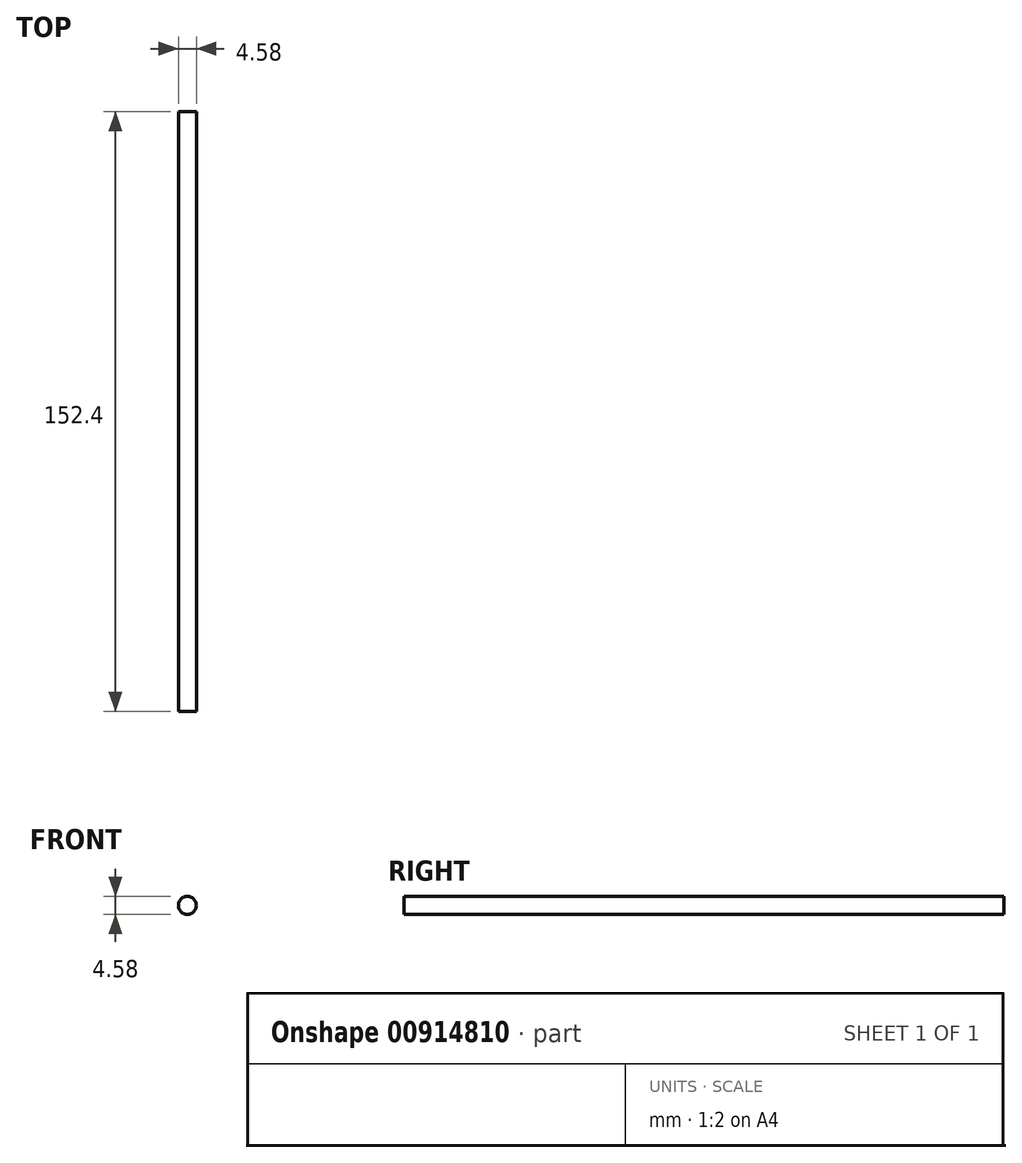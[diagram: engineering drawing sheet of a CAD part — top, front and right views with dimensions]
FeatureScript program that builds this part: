
annotation { "Feature Type Name" : "Feature", "Feature Type Description" : "" }
export const myFeature = defineFeature(function(context is Context, id is Id, definition is map)
    precondition{}
    {
        {
            var Q0;
            Q0=qCreatedBy(makeId("Front.planeOp"),FACE);
            var sketch = newSketch(context, id + "F0", { "sketchPlane" : qUnion([Q0])});
            skCircle(sketch, "E0", {"center": v(0, 0) * mm, "radius": 2.29 * mm});
            skSolve(sketch);
        }
        {
            var Q0;
            Q0=makeQuery(id+"F0.imprint","IMPRINT",FACE,{"disambiguationData":[TD([[makeQuery(id+"F0.imprint","IMPRINT",EDGE,{"derivedFrom":sQuery(id+"F0.wireOp",EDGE,"E0")}),1.0]])]});
            extrude(context, id + "F1", {"entities" : qUnion([Q0]), "depth" : 152.4 * mm, "offsetDistance" : 25.4 * mm});
        }
    });
